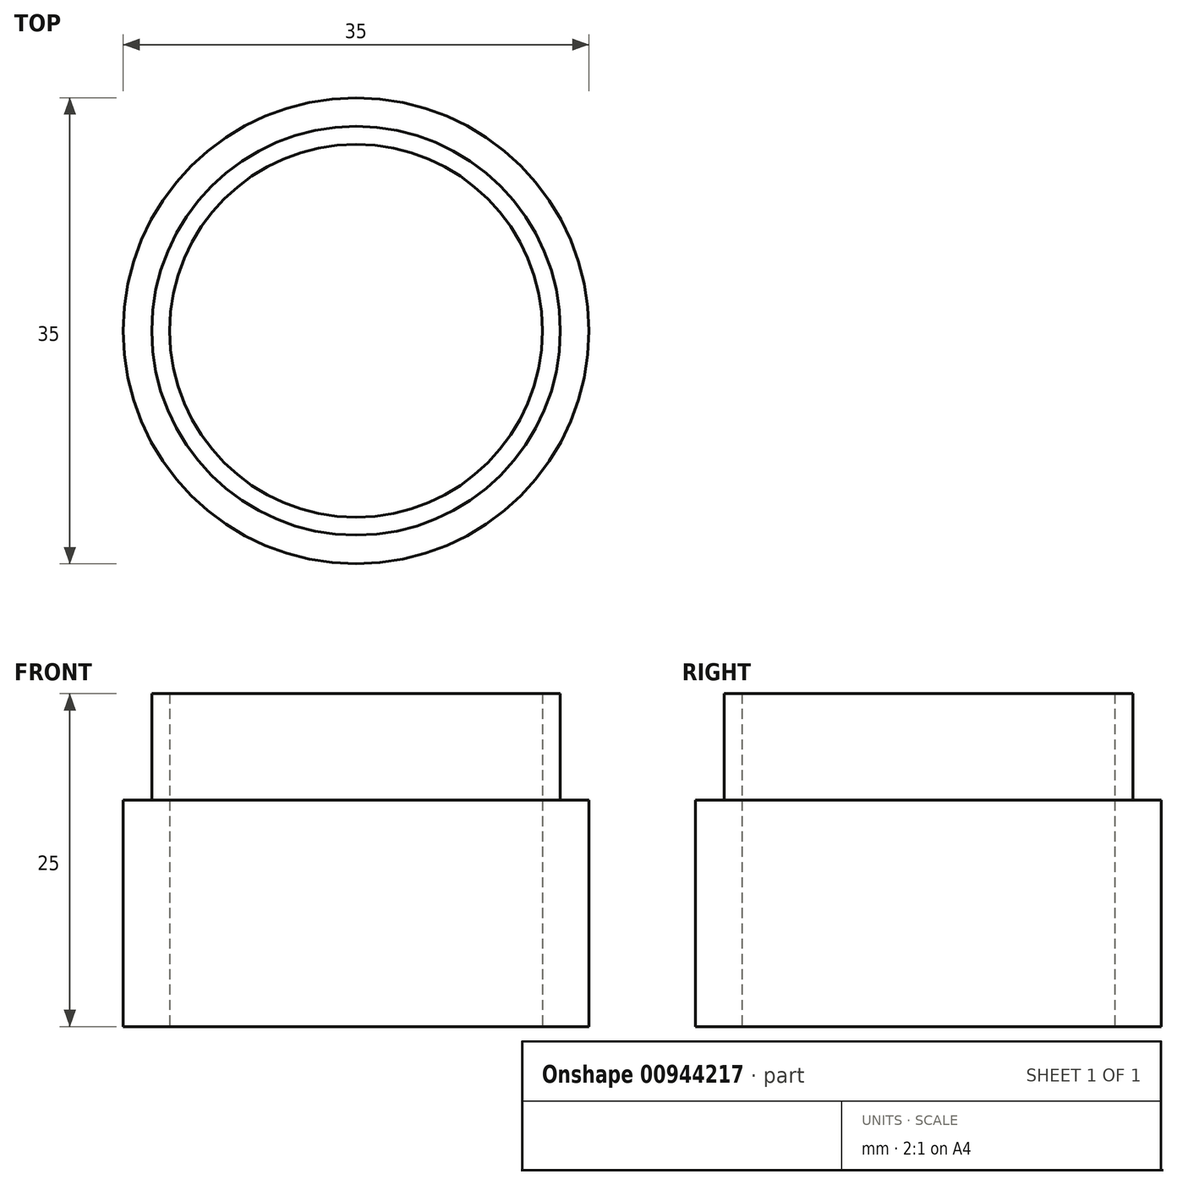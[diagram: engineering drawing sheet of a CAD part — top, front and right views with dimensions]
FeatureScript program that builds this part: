
annotation { "Feature Type Name" : "Feature", "Feature Type Description" : "" }
export const myFeature = defineFeature(function(context is Context, id is Id, definition is map)
    precondition{}
    {
        {
            var Q0;
            Q0=qCreatedBy(makeId("Front.planeOp"),FACE);
            var sketch = newSketch(context, id + "F0", { "sketchPlane" : qUnion([Q0])});
            skLineSegment(sketch, "E0", {"start": v(0, 0) * mm, "end": v(0, 25) * mm, "construction": true});
            skLineSegment(sketch, "E1", {"start": v(-14, 25) * mm, "end": v(-14, 0) * mm});
            skLineSegment(sketch, "E2", {"start": v(-14, 0) * mm, "end": v(-17.5, 0) * mm});
            skLineSegment(sketch, "E3", {"start": v(-17.5, 0) * mm, "end": v(-17.5, 17) * mm});
            skLineSegment(sketch, "E4", {"start": v(-17.5, 17) * mm, "end": v(-15.35, 17) * mm});
            skLineSegment(sketch, "E5", {"start": v(-15.35, 17) * mm, "end": v(-15.35, 25) * mm});
            skLineSegment(sketch, "E6", {"start": v(-15.35, 25) * mm, "end": v(-14, 25) * mm});
            skSolve(sketch);
        }
        {
            var Q0;
            Q0=makeQuery(id+"F0.imprint","IMPRINT",FACE,{"disambiguationData":[TD([[makeQuery(id+"F0.imprint","IMPRINT",EDGE,{"derivedFrom":sQuery(id+"F0.wireOp",EDGE,"E1")}),-1.0]])]});
            var Q1;
            Q1=sQuery(id+"F0.wireOp",EDGE,"E0");
            revolve(context, id + "F1", {"surfaceOperationType" : NewSurfaceOperationType.NEW, "entities" : qUnion([Q0]), "axis" : qUnion([Q1]), "revolveType" : RevolveType.FULL});
        }
    });
